# Revit family: 3031816 Lighting Fixture_Sylvania_Syl-Lighter II_Ceiling Recessed
name_source: partatom
category: Lighting Fixtures
revit_build: Autodesk Revit 2017 (Build: 20190507_1515(x64)
units: mm (PartAtom-declared; Revit-internal decimal feet)

## family parameters
Cut with Voids When Loaded = No
Host = Face
Light Source = Yes
OmniClass Number = 23.80.70.11.17
OmniClass Title = Specialized Lighting by Location or Use
Part Type = Normal
Room Calculation Point = No
Round Connector Dimension = Use Diameter
Shared = No

## types (1)
- Syl-Lighter LED II 220 RO 21W WW
    Accessory Diameter = 220 mm  [stored 0.721785 ft]
    Accessory Material = Aluminum_Sylvania_Syl-Lighter LED II_White_RAL 9003
    Accessory Radius = 110 mm  [stored 0.360892 ft]
    Apparent Load = 21 VA
    Assembly Code = D5020200
    Beam Angle = 74.00°
    Body Material = Metal_Sylvania_Syl-Lighter LED II_Silver
    Catalog Number = 3031816 Syl-Lighter LED II 220 RO 21W WW
    Color Filter = 16777215
    Cutout Diameter = 205 mm  [stored 0.672572 ft]
    Default Elevation = 0 mm  [stored 0 ft]
    Description = Syl-Lighter LED II is available in 4 different round body sizes: 165mm, 195mm, 220mm & 240mm Syl-Lighter LED II 165 12W delivers a 1,134 lumen output (4,000K) - perfect for 1x26W CFL replacement Syl-Lighter LED II 195 15W delivers a 1,480 lumen output (4,000K) - perfect for 1x32W/2x18W CFL replacement Syl-Lighter LED II 220 21W delivers a 1,989 lumen output (4,000K) - perfect for 1x42W CFL replacement Syl-Lighter LED II 240 25W delivers a 2,289 lumen output (4,000K)- perfect for 2x26W CFL replacement High efficacy up to 99lm/W (Syl-Lighter LED II 195 4,000K) IP44 rating allows for installation in applicable wet zone areas Choice of 3,000K (warm white) or 4,000K (neutral white) Shallow recess depth of <65mm Can replace existing large CFL downlights using a 225mm ceiling cut out (Syl-Lighter LED II 240) Energy efficient electronic gear including analogue 1-10V and DALI dimmable options IK07 polycarbonate diffuser allows for a wider light distribution than a reflector downlight, allowing for increased spacings between luminaires 3 hour emergency pack available (to be ordered in addition to the luminaire) Ideal for applications such as corridors, public WCs and back of house areas Quick and easy to install Loop in-Loop out facility with red push fit terminal block for quick wiring White bezel (RAL 9003) Energy Class: A++, A+, A Long lifetime: 50,000 hours life at L70 (L80: 30,000 hours, L90: 15,000 hours)
    Diameter = 205 mm  [stored 0.672572 ft]
    Diffuser Diameter = 185 mm  [stored 0.606955 ft]
    Diffuser Material = Polycarbonate_Sylvania_Syl-Lighter LED II_Opal
    Diffuser Radius = 92.5 mm  [stored 0.303478 ft]
    Dimmable = DALI
    Dimming Lamp Color Temperature Shift = <None>
    Drive Current = 450mA
    Electrical Protection = CLASS II
    Emit Shape Visible in Rendering = No
    Emit from Circle Diameter = 185 mm  [stored 0.606955 ft]
    Energy Class = A++, A+, A
    Glow Wire Test = 650 °C
    Height = 60 mm  [stored 0.19685 ft]
    IK Rating = IK07
    IP Rating = IP44
    Inner Diameter = 201 mm  [stored 0.659449 ft]
    Lamp = LED
    Lamp Comments = Integrated LED
    Life = 50 000h
    Manufacturer = Feilo Sylvania
    Model = Syl-Lighter LED II 220 RO 21W WW
    Photometric Web File = 3031816_Syl-Lighter220LED21WWW-182064.ies
    Product Family = SYL-LIGHTER LED II
    Product Page URL = http://www.sylvania-lighting.com
    Recessed Depth = 60 mm  [stored 0.19685 ft]
    Ta Rating = -10°C to +40°C
    Tilt Angle = -90.00°
    URL = http://www.sylvania-lighting.com
    Voltage = 240 V
    Voltage Comments = UNV (Universal Voltage; 220-240 Volt)
    Weight = 0.60 kg

note: [stored X ft] marks values corroborated as IEEE doubles in the binary element streams (Revit-internal decimal feet)

## geometry (parser evidence)
native form markers: Blend x4, Sweep x1
no freeform markers — native parametric forms only
